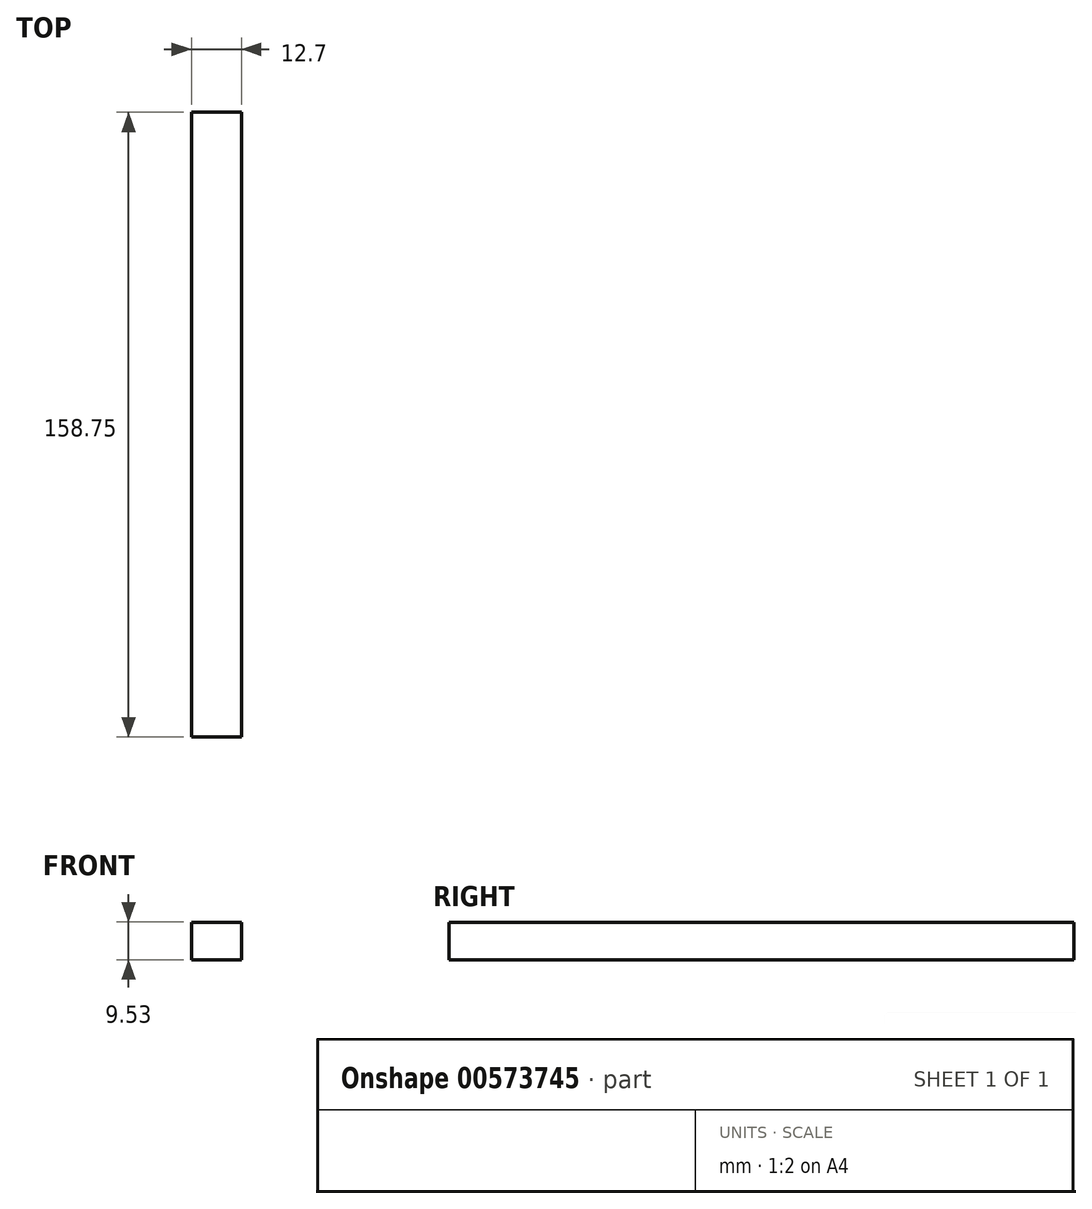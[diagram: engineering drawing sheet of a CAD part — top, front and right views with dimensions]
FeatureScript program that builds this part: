
annotation { "Feature Type Name" : "Feature", "Feature Type Description" : "" }
export const myFeature = defineFeature(function(context is Context, id is Id, definition is map)
    precondition{}
    {
        {
            var Q0;
            Q0=qCreatedBy(makeId("Top.planeOp"),FACE);
            var sketch = newSketch(context, id + "F0", { "sketchPlane" : qUnion([Q0])});
            skLineSegment(sketch, "E0.bottom", {"start": v(0, 0) * mm, "end": v(12.7, 0) * mm});
            skLineSegment(sketch, "E0.top", {"start": v(0, -158.75) * mm, "end": v(12.7, -158.75) * mm});
            skLineSegment(sketch, "E0.left", {"start": v(0, 0) * mm, "end": v(0, -158.75) * mm});
            skLineSegment(sketch, "E0.right", {"start": v(12.7, 0) * mm, "end": v(12.7, -158.75) * mm});
            skSolve(sketch);
        }
        {
            var Q0;
            Q0=makeQuery(id+"F0.imprint","IMPRINT",FACE,{"disambiguationData":[TD([[makeQuery(id+"F0.imprint","IMPRINT",EDGE,{"derivedFrom":sQuery(id+"F0.wireOp",EDGE,"E0.bottom")}),-1.0]])]});
            extrude(context, id + "F1", {"entities" : qUnion([Q0]), "depth" : 9.52 * mm, "offsetDistance" : 25.4 * mm});
        }
    });
